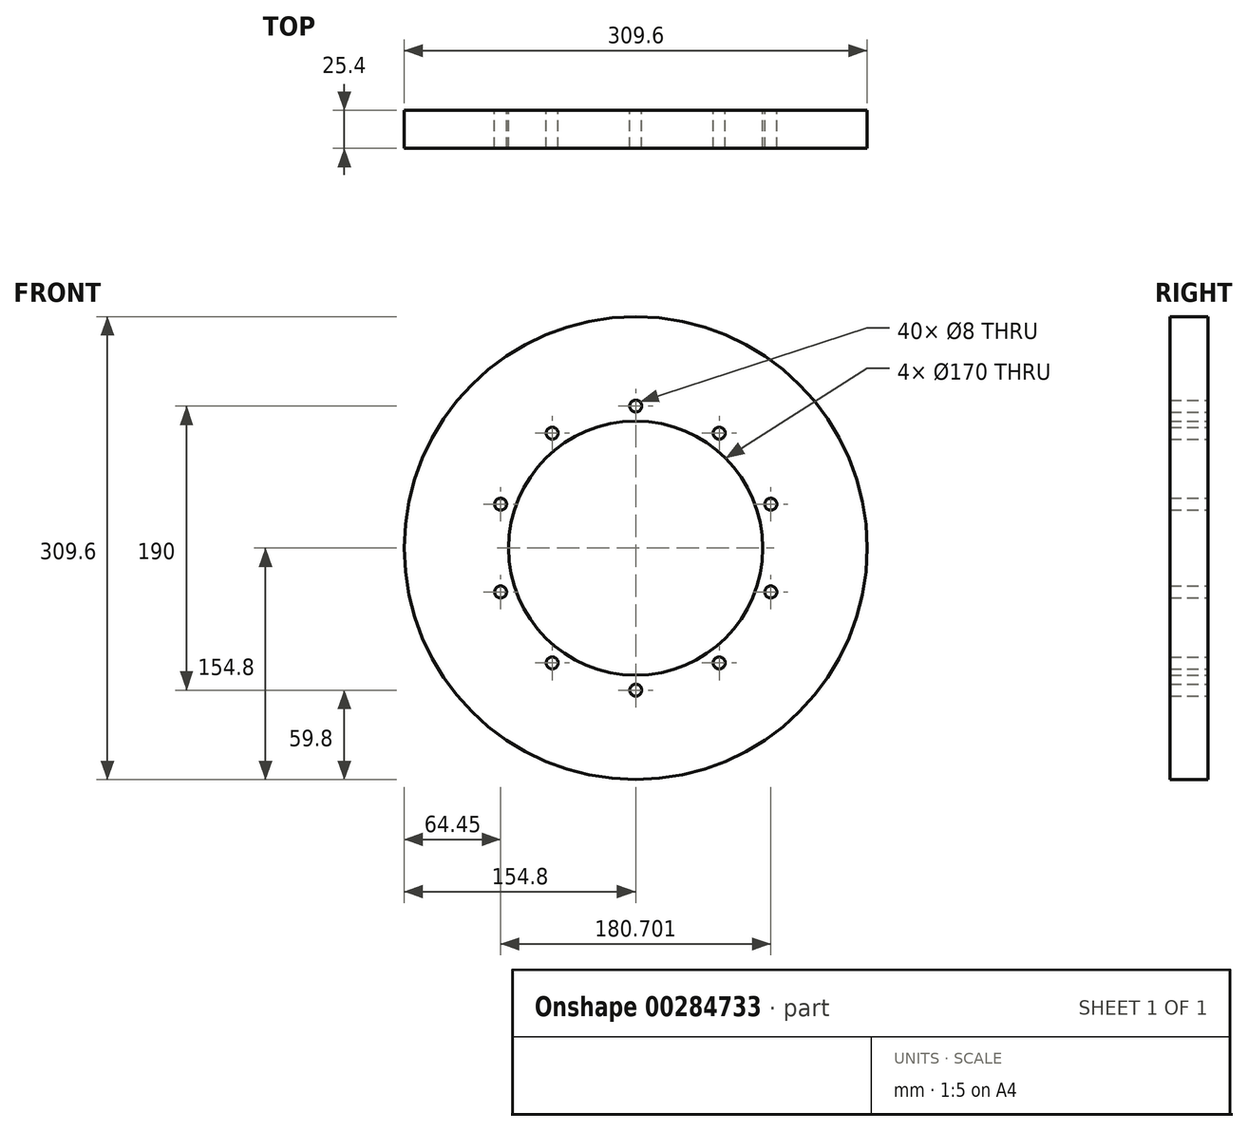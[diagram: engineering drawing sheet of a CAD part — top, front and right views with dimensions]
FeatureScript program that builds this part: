
annotation { "Feature Type Name" : "Feature", "Feature Type Description" : "" }
export const myFeature = defineFeature(function(context is Context, id is Id, definition is map)
    precondition{}
    {
        {
            var Q0;
            Q0=qCreatedBy(makeId("Front.planeOp"),FACE);
            var sketch = newSketch(context, id + "F0", { "sketchPlane" : qUnion([Q0])});
            skCircle(sketch, "E0", {"center": v(0, 0) * mm, "radius": 154.8 * mm});
            skCircle(sketch, "E1", {"center": v(0, 0) * mm, "radius": 85 * mm});
            skCircle(sketch, "E2", {"center": v(0, 0) * mm, "radius": 95 * mm, "construction": true});
            skPoint(sketch, "E3", {"position": v(0, 95) * mm});
            skCircle(sketch, "E4", {"center": v(0, 95) * mm, "radius": 4 * mm});
            skCircle(sketch, "E5.1.0", {"center": v(-55.84, 76.86) * mm, "radius": 4 * mm});
            skCircle(sketch, "E5.2.0", {"center": v(-90.35, 29.36) * mm, "radius": 4 * mm});
            skCircle(sketch, "E5.3.0", {"center": v(-90.35, -29.36) * mm, "radius": 4 * mm});
            skCircle(sketch, "E5.4.0", {"center": v(-55.84, -76.86) * mm, "radius": 4 * mm});
            skCircle(sketch, "E5.5.0", {"center": v(0, -95) * mm, "radius": 4 * mm});
            skCircle(sketch, "E5.6.0", {"center": v(55.84, -76.86) * mm, "radius": 4 * mm});
            skCircle(sketch, "E5.7.0", {"center": v(90.35, -29.36) * mm, "radius": 4 * mm});
            skCircle(sketch, "E5.8.0", {"center": v(90.35, 29.36) * mm, "radius": 4 * mm});
            skCircle(sketch, "E5.9.0", {"center": v(55.84, 76.86) * mm, "radius": 4 * mm});
            skSolve(sketch);
        }
        {
            var Q0;
            Q0=qSketchRegion(id+"F0",true);
            extrude(context, id + "F1", {"entities" : qUnion([Q0]), "depth" : 25.4 * mm});
        }
    });
